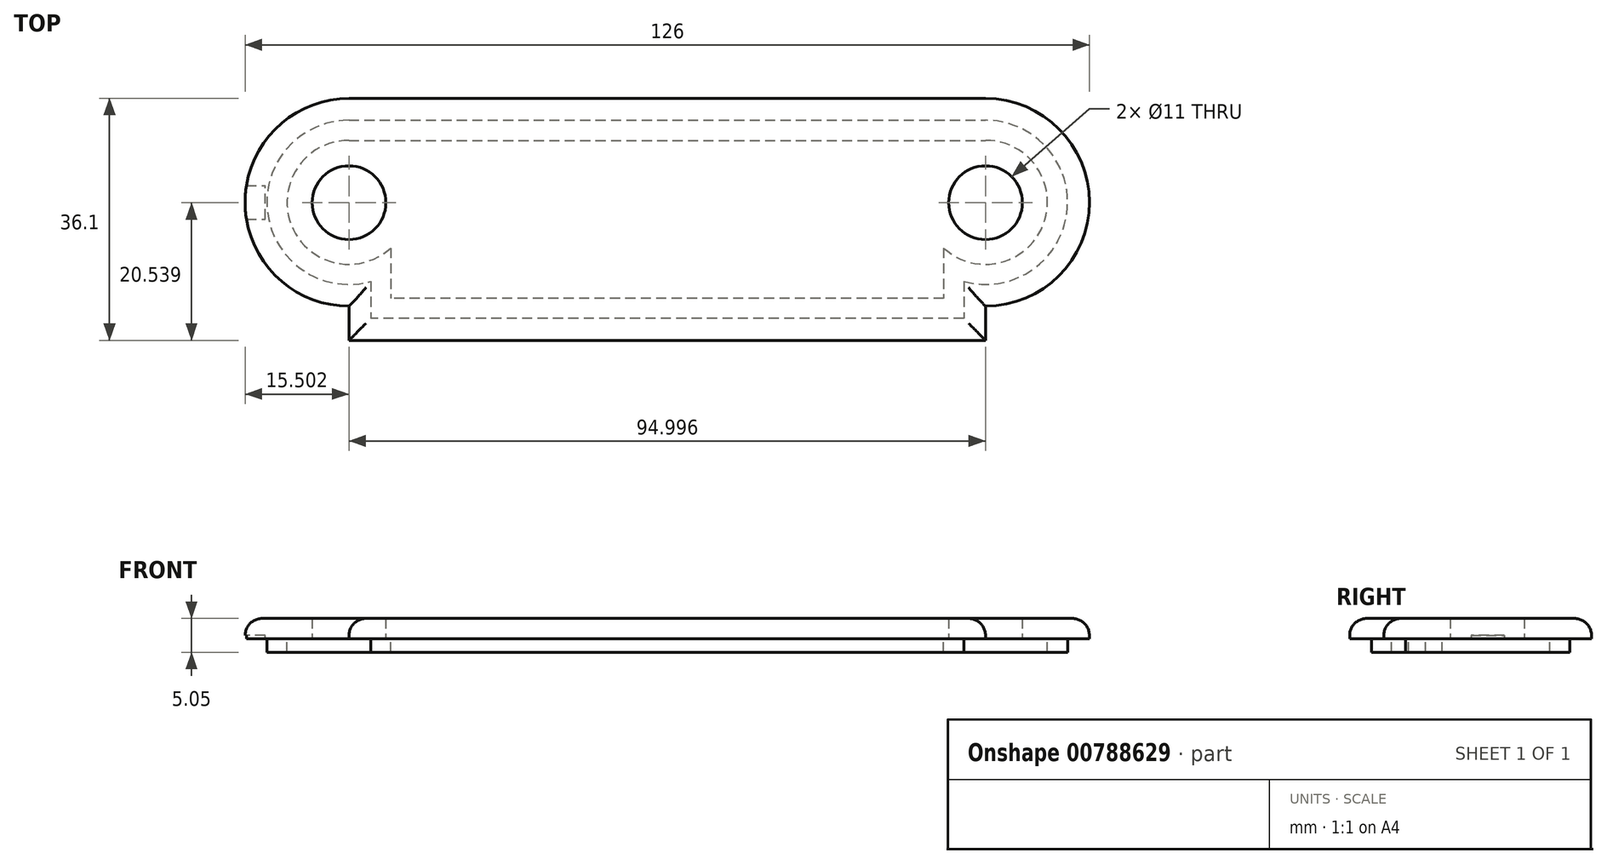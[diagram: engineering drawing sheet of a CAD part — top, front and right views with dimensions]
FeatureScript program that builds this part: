
annotation { "Feature Type Name" : "Feature", "Feature Type Description" : "" }
export const myFeature = defineFeature(function(context is Context, id is Id, definition is map)
    precondition{}
    {
        {
            var Q0;
            Q0=qCreatedBy(makeId("Top.planeOp"),FACE);
            var sketch = newSketch(context, id + "F0", { "sketchPlane" : qUnion([Q0])});
            skLineSegment(sketch, "E0.bottom", {"start": v(47.5, 18.05) * mm, "end": v(-47.5, 18.05) * mm});
            skLineSegment(sketch, "E0.top", {"start": v(47.5, -18.05) * mm, "end": v(-47.5, -18.05) * mm});
            skLineSegment(sketch, "E0.left", {"start": v(47.5, 18.05) * mm, "end": v(47.5, -18.05) * mm});
            skLineSegment(sketch, "E0.right", {"start": v(-47.5, 18.05) * mm, "end": v(-47.5, -18.05) * mm});
            skPoint(sketch, "E0.middle", {"position": v(0, 0) * mm});
            skCircle(sketch, "E1", {"center": v(-47.5, 2.55) * mm, "radius": 15.5 * mm});
            skCircle(sketch, "E2", {"center": v(47.5, 2.55) * mm, "radius": 15.5 * mm});
            skSolve(sketch);
        }
        {
            var Q0;
            Q0=qSketchRegion(id+"F0",true);
            extrude(context, id + "F1", {"entities" : qUnion([Q0]), "depth" : 3.05 * mm, "offsetDistance" : 25.4 * mm});
        }
        {
            var Q0;
            Q0=makeQuery(id+"F1.opExtrude","CAP_EDGE",EDGE,{"disambiguationData":[OSD([sQuery(id+"F0.wireOp",EDGE,"E1")])],"isStart":false});
            var Q1;
            Q1=makeQuery(id+"F1.opExtrude","CAP_EDGE",EDGE,{"disambiguationData":[OSD([sQuery(id+"F0.wireOp",EDGE,"E2")])],"isStart":false});
            var Q2;
            Q2=makeQuery(id+"F1.opExtrude","CAP_FACE",FACE,{"disambiguationData":[OSD([sQuery(id+"F0.wireOp",EDGE,"E0.bottom"),sQuery(id+"F0.wireOp",EDGE,"E0.top"),sQuery(id+"F0.wireOp",EDGE,"E0.left"),sQuery(id+"F0.wireOp",EDGE,"E0.right"),sQuery(id+"F0.wireOp",EDGE,"E1"),sQuery(id+"F0.wireOp",EDGE,"E2")])],"isStart":false});
            fillet(context, id + "F2", {"entities" : qUnion([Q0, Q1, Q2]), "radius" : 2.54 * mm, "tangentPropagation" : true, "allowEdgeOverflow" : false});
        }
        {
            var Q0;
            Q0=qCreatedBy(makeId("Top.planeOp"),FACE);
            var sketch = newSketch(context, id + "F3", { "sketchPlane" : qUnion([Q0])});
            skCircle(sketch, "E3", {"center": v(-47.5, 2.49) * mm, "radius": 5.5 * mm});
            skCircle(sketch, "E4", {"center": v(47.5, 2.49) * mm, "radius": 5.5 * mm});
            skSolve(sketch);
        }
        {
            var Q0;
            Q0=qSketchRegion(id+"F3",true);
            extrude(context, id + "F4", {"entities" : qUnion([Q0]), "operationType" : NewBodyOperationType.REMOVE, "depth" : 3.05 * mm, "offsetDistance" : 25.4 * mm});
        }
        {
            var Q0;
            Q0=qCreatedBy(makeId("Top.planeOp"),FACE);
            var sketch = newSketch(context, id + "F5", { "sketchPlane" : qUnion([Q0])});
            skLineSegment(sketch, "E5.left", {"start": v(47.5, 2.55) * mm, "end": v(47.5, 2.52) * mm});
            skPoint(sketch, "E5.middle", {"position": v(0, 0) * mm});
            skPoint(sketch, "E6.end.orphan", {"position": v(-47.5, 2.55) * mm});
            skLineSegment(sketch, "E7", {"start": v(47.5, 18.05) * mm, "end": v(47.5, 18.05) * mm});
            skLineSegment(sketch, "E8", {"start": v(47.5, 2.52) * mm, "end": v(47.5, 2.52) * mm});
            skArc(sketch, "E9.0", {"start": v(-47.5, 14.8) * mm, "mid": v(-59.64, 0.9) * mm, "end": v(-44.25, -9.26) * mm});
            skArc(sketch, "E9.1", {"start": v(44.25, -9.26) * mm, "mid": v(59.64, 0.9) * mm, "end": v(47.5, 14.8) * mm});
            skLineSegment(sketch, "E9.2", {"start": v(44.25, -9.26) * mm, "end": v(44.25, -14.8) * mm});
            skLineSegment(sketch, "E9.3", {"start": v(44.25, -14.8) * mm, "end": v(-44.25, -14.8) * mm});
            skLineSegment(sketch, "E9.4", {"start": v(-44.25, -9.26) * mm, "end": v(-44.25, -14.8) * mm});
            skLineSegment(sketch, "E10", {"start": v(-47.5, 14.8) * mm, "end": v(47.5, 14.8) * mm});
            skLineSegment(sketch, "E11.0", {"start": v(41.25, -4.27) * mm, "end": v(41.25, -11.8) * mm});
            skLineSegment(sketch, "E11.1", {"start": v(-41.25, -4.27) * mm, "end": v(-41.25, -11.8) * mm});
            skArc(sketch, "E11.2", {"start": v(-47.5, 11.8) * mm, "mid": v(-56.12, -0.8) * mm, "end": v(-41.25, -4.27) * mm});
            skLineSegment(sketch, "E11.3", {"start": v(41.25, -11.8) * mm, "end": v(-41.25, -11.8) * mm});
            skLineSegment(sketch, "E11.4", {"start": v(-47.5, 11.8) * mm, "end": v(47.5, 11.8) * mm});
            skArc(sketch, "E11.5", {"start": v(41.25, -4.27) * mm, "mid": v(56.12, -0.8) * mm, "end": v(47.5, 11.8) * mm});
            skSolve(sketch);
        }
        {
            var Q0;
            Q0=makeQuery(id+"F5.imprint","IMPRINT",FACE,{"disambiguationData":[TD([[makeQuery(id+"F5.imprint","IMPRINT",EDGE,{"derivedFrom":sQuery(id+"F5.wireOp",EDGE,"E9.0")}),1.0]])]});
            extrude(context, id + "F6", {"entities" : qUnion([Q0]), "operationType" : NewBodyOperationType.ADD, "oppositeDirection" : true, "depth" : 2 * mm, "offsetDistance" : 25.4 * mm});
        }
        {
            var Q0;
            Q0=qCreatedBy(makeId("Right.planeOp"),FACE);
            cPlane(context, id + "F7", {"entities" : qUnion([Q0]), "cplaneType" : CPlaneType.OFFSET, "offset" : 63 * mm, "oppositeDirection" : true, "width" : 152.4 * mm, "height" : 152.4 * mm});
        }
        {
            var Q0;
            Q0=qCreatedBy(id+"F7.planeOp",FACE);
            var sketch = newSketch(context, id + "F8", { "sketchPlane" : qUnion([Q0])});
            skLineSegment(sketch, "E12.bottom", {"start": v(0.05, -0.5) * mm, "end": v(5.05, -0.5) * mm});
            skLineSegment(sketch, "E12.top", {"start": v(0.05, 0.5) * mm, "end": v(5.05, 0.5) * mm});
            skLineSegment(sketch, "E12.left", {"start": v(0.05, -0.5) * mm, "end": v(0.05, 0.5) * mm});
            skLineSegment(sketch, "E12.right", {"start": v(5.05, -0.5) * mm, "end": v(5.05, 0.5) * mm});
            skPoint(sketch, "E12.middle", {"position": v(2.55, 0) * mm});
            skSolve(sketch);
        }
        {
            var Q0;
            Q0=qSketchRegion(id+"F8",true);
            extrude(context, id + "F9", {"entities" : qUnion([Q0]), "operationType" : NewBodyOperationType.REMOVE, "depth" : 3 * mm, "offsetDistance" : 25.4 * mm});
        }
    });
